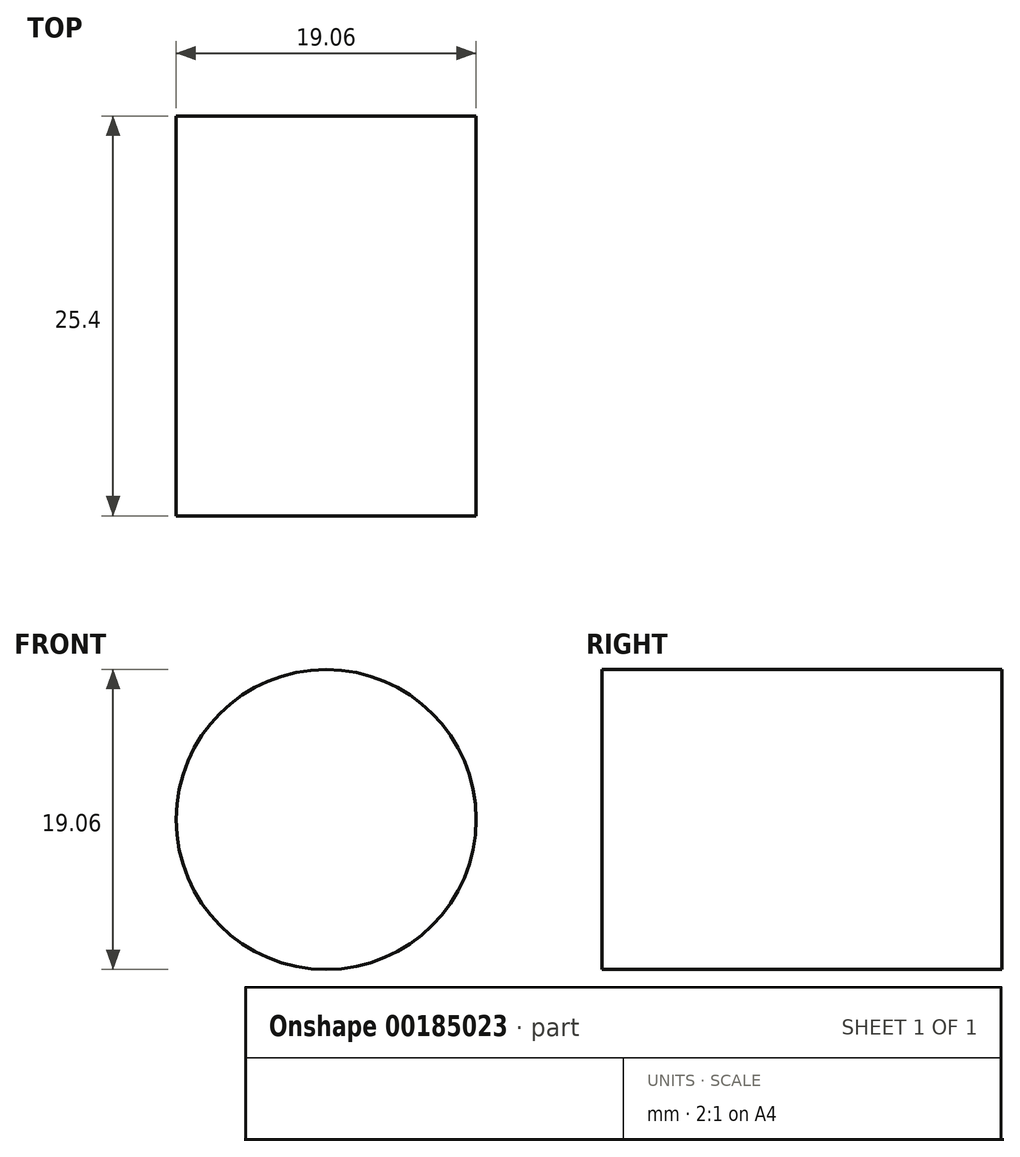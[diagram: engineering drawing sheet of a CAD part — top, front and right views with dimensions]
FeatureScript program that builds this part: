
annotation { "Feature Type Name" : "Feature", "Feature Type Description" : "" }
export const myFeature = defineFeature(function(context is Context, id is Id, definition is map)
    precondition{}
    {
        {
            var Q0;
            Q0=qCreatedBy(makeId("Front.planeOp"),FACE);
            var sketch = newSketch(context, id + "F0", { "sketchPlane" : qUnion([Q0])});
            skCircle(sketch, "E0", {"center": v(0, 0) * mm, "radius": 9.53 * mm});
            skSolve(sketch);
        }
        {
            var Q0;
            Q0 = qSketchRegion(id + "F0", true);
            extrude(context, id + "F1", {"entities" : qUnion([Q0]), "depth" : 25.4 * mm});
        }
        {
            var Q0;
            Q0=qCreatedBy(makeId("Front.planeOp"),FACE);
            var sketch = newSketch(context, id + "F2", { "sketchPlane" : qUnion([Q0])});
            skLineSegment(sketch, "E1.bottom", {"start": v(4.76, -4.76) * mm, "end": v(-4.76, -4.76) * mm});
            skLineSegment(sketch, "E1.top", {"start": v(4.76, 4.76) * mm, "end": v(-4.76, 4.76) * mm});
            skLineSegment(sketch, "E1.left", {"start": v(4.76, -4.76) * mm, "end": v(4.76, 4.76) * mm});
            skLineSegment(sketch, "E1.right", {"start": v(-4.76, -4.76) * mm, "end": v(-4.76, 4.76) * mm});
            skPoint(sketch, "E1.middle", {"position": v(0, 0) * mm});
            skCircle(sketch, "E2", {"center": v(0, 0) * mm, "radius": 4.76 * mm});
            skSolve(sketch);
        }
        {
            var Q0;
            {var subQ0=sQuery(id+"F2.wireOp",EDGE,"E2");var subQ1=makeQuery(id+"F2.imprint","INTERSECT",VERTEX,{"derivedFrom":[sQuery(id+"F2.wireOp",EDGE,"E1.top"),subQ0]});Q0=makeQuery(id+"F2.imprint","IMPRINT",FACE,{"disambiguationData":[TD([[makeQuery(id+"F2.imprint","IMPRINT",EDGE,{"disambiguationData":[TD([[subQ1,1.0]])],"derivedFrom":subQ0}),1.0]])]});}
            extrude(context, id + "F3", {"entities" : qUnion([Q0]), "operationType" : NewBodyOperationType.REMOVE, "endBound" : BoundingType.THROUGH_ALL, "oppositeDirection" : true, "depth" : 25.4 * mm});
        }
    });
